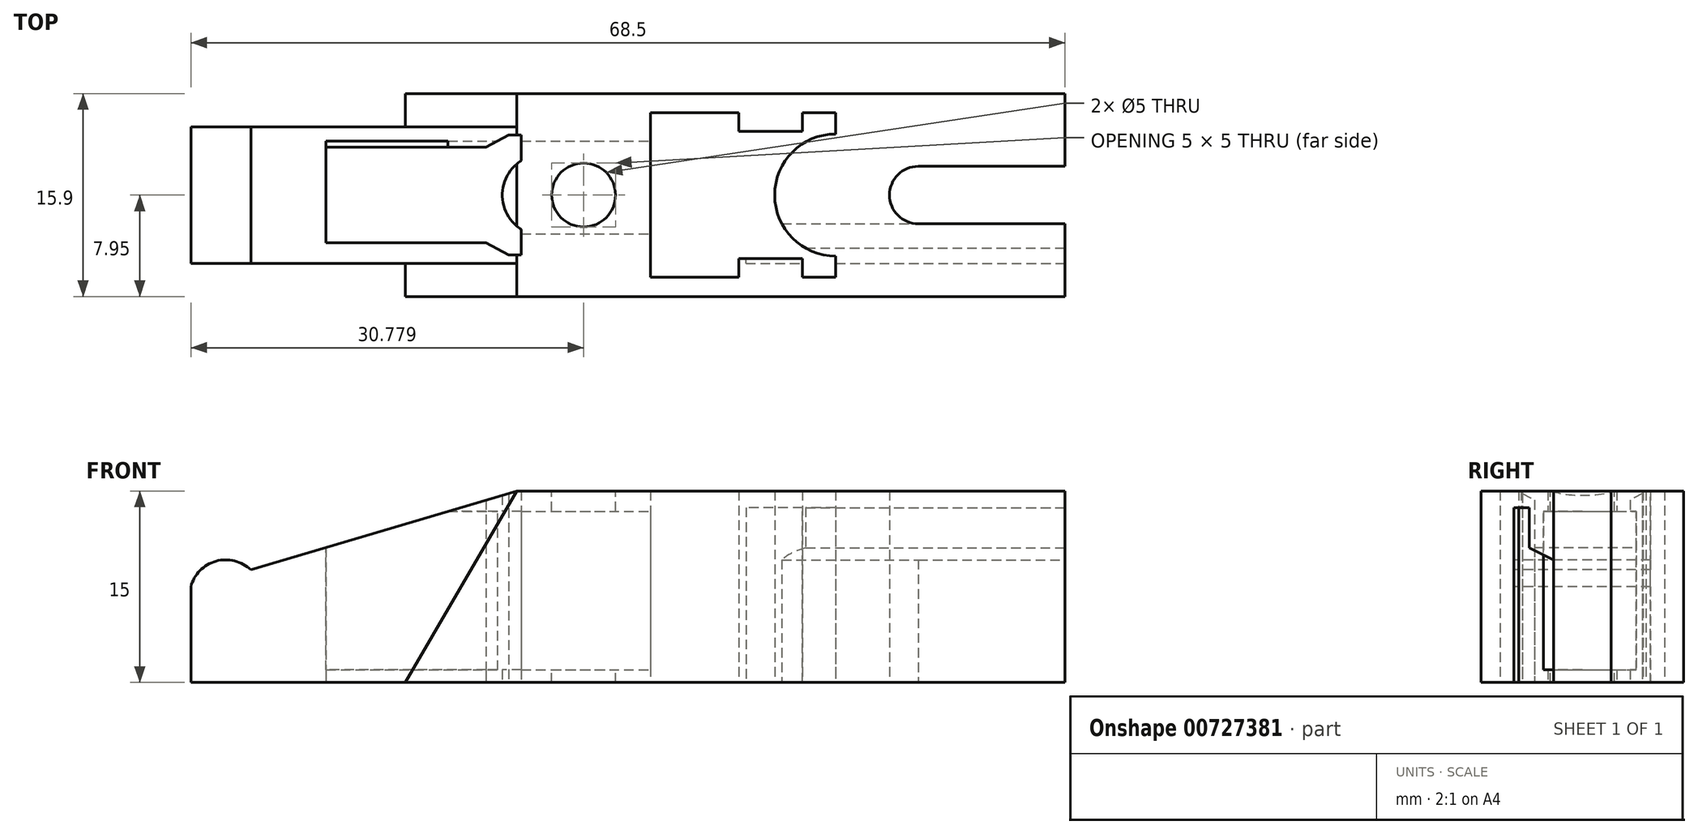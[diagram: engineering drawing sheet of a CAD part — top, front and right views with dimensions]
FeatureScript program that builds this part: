
annotation { "Feature Type Name" : "Feature", "Feature Type Description" : "" }
export const myFeature = defineFeature(function(context is Context, id is Id, definition is map)
    precondition{}
    {
        {
            var Q0;
            Q0=qCreatedBy(makeId("Top.planeOp"),FACE);
            var sketch = newSketch(context, id + "F0", { "sketchPlane" : qUnion([Q0])});
            skLineSegment(sketch, "E0", {"start": v(0, 0) * mm, "end": v(0, 10.7) * mm});
            skLineSegment(sketch, "E1", {"start": v(0, 10.7) * mm, "end": v(16.8, 10.7) * mm});
            skLineSegment(sketch, "E2", {"start": v(68.5, 13.3) * mm, "end": v(68.5, 7.6) * mm});
            skLineSegment(sketch, "E3", {"start": v(68.5, 7.6) * mm, "end": v(57, 7.6) * mm});
            skLineSegment(sketch, "E4", {"start": v(57, 3.1) * mm, "end": v(68.5, 3.1) * mm});
            skLineSegment(sketch, "E5", {"start": v(0, 0) * mm, "end": v(16.8, 0) * mm});
            skLineSegment(sketch, "E6", {"start": v(16.8, 0) * mm, "end": v(16.8, -2.6) * mm});
            skLineSegment(sketch, "E7", {"start": v(16.8, -2.6) * mm, "end": v(68.5, -2.6) * mm});
            skLineSegment(sketch, "E8", {"start": v(68.5, -2.6) * mm, "end": v(68.5, 3.1) * mm});
            skLineSegment(sketch, "E9", {"start": v(50.53, -1.1) * mm, "end": v(50.53, 0.57) * mm});
            skLineSegment(sketch, "E10", {"start": v(25.9, 0.66) * mm, "end": v(25.9, 2.66) * mm});
            skLineSegment(sketch, "E11.MirrorCS", {"start": v(10.6, 9.1) * mm, "end": v(23.13, 9.1) * mm});
            skLineSegment(sketch, "E12.MirrorCS", {"start": v(25.9, 10.04) * mm, "end": v(25.9, 8.04) * mm});
            skArc(sketch, "E13", {"start": v(25.9, 8.04) * mm, "mid": v(24.4, 5.35) * mm, "end": v(25.9, 2.66) * mm});
            skLineSegment(sketch, "E14.MirrorCS", {"start": v(16.8, 10.7) * mm, "end": v(16.8, 13.3) * mm});
            skLineSegment(sketch, "E15.MirrorCS", {"start": v(16.8, 13.3) * mm, "end": v(68.5, 13.3) * mm});
            skLineSegment(sketch, "E16", {"start": v(36.03, -1.1) * mm, "end": v(42.93, -1.1) * mm});
            skLineSegment(sketch, "E17", {"start": v(42.93, -1.1) * mm, "end": v(42.93, 0.37) * mm});
            skLineSegment(sketch, "E18", {"start": v(42.93, 0.37) * mm, "end": v(47.93, 0.37) * mm});
            skLineSegment(sketch, "E19", {"start": v(47.93, 0.37) * mm, "end": v(47.93, -1.1) * mm});
            skLineSegment(sketch, "E20", {"start": v(47.93, -1.1) * mm, "end": v(50.53, -1.1) * mm});
            skLineSegment(sketch, "E21.MirrorCS", {"start": v(23.13, 9.1) * mm, "end": v(24.9, 10.04) * mm});
            skLineSegment(sketch, "E22.MirrorCS", {"start": v(24.9, 10.04) * mm, "end": v(25.9, 10.04) * mm});
            skPoint(sketch, "E23", {"position": v(24.4, 5.35) * mm});
            skLineSegment(sketch, "E24", {"start": v(57, 7.6) * mm, "end": v(57, 3.1) * mm, "construction": true});
            skArc(sketch, "E25", {"start": v(57, 7.6) * mm, "mid": v(54.75, 5.35) * mm, "end": v(57, 3.1) * mm});
            skLineSegment(sketch, "E26", {"start": v(0, 5.35) * mm, "end": v(68.5, 5.35) * mm, "construction": true});
            skLineSegment(sketch, "E27.MirrorCS", {"start": v(10.6, 1.6) * mm, "end": v(23.13, 1.6) * mm});
            skLineSegment(sketch, "E28.MirrorCS", {"start": v(23.13, 1.6) * mm, "end": v(24.9, 0.66) * mm});
            skLineSegment(sketch, "E29.MirrorCS", {"start": v(24.9, 0.66) * mm, "end": v(25.9, 0.66) * mm});
            skLineSegment(sketch, "E30", {"start": v(10.6, 9.1) * mm, "end": v(10.6, 1.6) * mm});
            skLineSegment(sketch, "E31", {"start": v(36.03, 11.8) * mm, "end": v(36.03, -1.1) * mm});
            skLineSegment(sketch, "E32.MirrorCS", {"start": v(36.03, 11.8) * mm, "end": v(42.93, 11.8) * mm});
            skLineSegment(sketch, "E33.MirrorCS", {"start": v(42.93, 11.8) * mm, "end": v(42.93, 10.33) * mm});
            skLineSegment(sketch, "E34.MirrorCS", {"start": v(42.93, 10.33) * mm, "end": v(47.93, 10.33) * mm});
            skLineSegment(sketch, "E35.MirrorCS", {"start": v(47.93, 10.33) * mm, "end": v(47.93, 11.8) * mm});
            skLineSegment(sketch, "E36.MirrorCS", {"start": v(47.93, 11.8) * mm, "end": v(50.53, 11.8) * mm});
            skLineSegment(sketch, "E37.MirrorCS", {"start": v(50.53, 11.8) * mm, "end": v(50.53, 10.13) * mm});
            skLineSegment(sketch, "E38", {"start": v(50.53, 10.13) * mm, "end": v(50.53, 0.57) * mm, "construction": true});
            skArc(sketch, "E39", {"start": v(50.53, 10.13) * mm, "mid": v(45.75, 5.35) * mm, "end": v(50.53, 0.57) * mm});
            skPoint(sketch, "E40", {"position": v(45.75, 5.35) * mm});
            skSolve(sketch);
        }
        {
            var Q0;
            Q0=qSketchRegion(id+"F0",true);
            var Q1;
            Q1=makeQuery(id+"F0.imprint","IMPRINT",FACE,{"disambiguationData":[TD([[makeQuery(id+"F0.imprint","IMPRINT",EDGE,{"derivedFrom":sQuery(id+"F0.wireOp",EDGE,"E0")}),-1.0]])]});
            extrude(context, id + "F1", {"entities" : qUnion([Q0, Q1]), "depth" : 15 * mm, "offsetDistance" : 25 * mm});
        }
        {
            var Q0;
            Q0=makeQuery(id+"F1.opExtrude","SWEPT_FACE",FACE,{"disambiguationData":[OSD([sQuery(id+"F0.wireOp",EDGE,"E7")])]});
            var sketch = newSketch(context, id + "F2", { "sketchPlane" : qUnion([Q0])});
            skLineSegment(sketch, "E41", {"start": v(16.8, 0) * mm, "end": v(25.53, 15) * mm});
            skLineSegment(sketch, "E42", {"start": v(25.53, 15) * mm, "end": v(16.8, 15) * mm});
            skLineSegment(sketch, "E43", {"start": v(16.8, 15) * mm, "end": v(16.8, 0) * mm});
            skSolve(sketch);
        }
        {
            var Q0;
            Q0=qSketchRegion(id+"F2",true);
            var Q1;
            Q1=makeQuery(id+"F1.opExtrude","SWEPT_FACE",FACE,{"disambiguationData":[OSD([sQuery(id+"F0.wireOp",EDGE,"E5")])]});
            extrude(context, id + "F3", {"entities" : qUnion([Q0]), "operationType" : NewBodyOperationType.REMOVE, "endBound" : BoundingType.UP_TO_SURFACE, "oppositeDirection" : true, "depth" : 25 * mm, "endBoundEntityFace" : qUnion([Q1]), "offsetDistance" : 25 * mm});
        }
        {
            var Q0;
            Q0=makeQuery(id+"F1.opExtrude","SWEPT_FACE",FACE,{"disambiguationData":[OSD([sQuery(id+"F0.wireOp",EDGE,"E15.MirrorCS")])]});
            var sketch = newSketch(context, id + "F4", { "sketchPlane" : qUnion([Q0])});
            skLineSegment(sketch, "E44", {"start": v(-16.8, 0) * mm, "end": v(-16.8, 15) * mm});
            skLineSegment(sketch, "E45", {"start": v(-16.8, 15) * mm, "end": v(-25.53, 15) * mm});
            skLineSegment(sketch, "E46", {"start": v(-25.53, 15) * mm, "end": v(-16.8, 0) * mm});
            skSolve(sketch);
        }
        {
            var Q0;
            Q0=qSketchRegion(id+"F4",true);
            var Q1;
            Q1=makeQuery(id+"F1.opExtrude","SWEPT_FACE",FACE,{"disambiguationData":[OSD([sQuery(id+"F0.wireOp",EDGE,"E1")])]});
            extrude(context, id + "F5", {"entities" : qUnion([Q0]), "operationType" : NewBodyOperationType.REMOVE, "endBound" : BoundingType.UP_TO_SURFACE, "oppositeDirection" : true, "depth" : 25 * mm, "endBoundEntityFace" : qUnion([Q1]), "offsetDistance" : 25 * mm});
        }
        {
            var Q0;
            Q0=makeQuery(id+"F1.opExtrude","CAP_FACE",FACE,{"disambiguationData":[OSD([sQuery(id+"F0.wireOp",EDGE,"E0"),sQuery(id+"F0.wireOp",EDGE,"E1"),sQuery(id+"F0.wireOp",EDGE,"E2"),sQuery(id+"F0.wireOp",EDGE,"E3"),sQuery(id+"F0.wireOp",EDGE,"E4"),sQuery(id+"F0.wireOp",EDGE,"E5"),sQuery(id+"F0.wireOp",EDGE,"E6"),sQuery(id+"F0.wireOp",EDGE,"E7"),sQuery(id+"F0.wireOp",EDGE,"E8"),sQuery(id+"F0.wireOp",EDGE,"E9"),sQuery(id+"F0.wireOp",EDGE,"E10"),sQuery(id+"F0.wireOp",EDGE,"E11.MirrorCS"),sQuery(id+"F0.wireOp",EDGE,"E12.MirrorCS"),sQuery(id+"F0.wireOp",EDGE,"E13"),sQuery(id+"F0.wireOp",EDGE,"E14.MirrorCS"),sQuery(id+"F0.wireOp",EDGE,"E15.MirrorCS"),sQuery(id+"F0.wireOp",EDGE,"E16"),sQuery(id+"F0.wireOp",EDGE,"E17"),sQuery(id+"F0.wireOp",EDGE,"E18"),sQuery(id+"F0.wireOp",EDGE,"E19"),sQuery(id+"F0.wireOp",EDGE,"E20"),sQuery(id+"F0.wireOp",EDGE,"E21.MirrorCS"),sQuery(id+"F0.wireOp",EDGE,"E22.MirrorCS"),sQuery(id+"F0.wireOp",EDGE,"E25"),sQuery(id+"F0.wireOp",EDGE,"E27.MirrorCS"),sQuery(id+"F0.wireOp",EDGE,"E28.MirrorCS"),sQuery(id+"F0.wireOp",EDGE,"E29.MirrorCS"),sQuery(id+"F0.wireOp",EDGE,"E30"),sQuery(id+"F0.wireOp",EDGE,"E31"),sQuery(id+"F0.wireOp",EDGE,"E32.MirrorCS"),sQuery(id+"F0.wireOp",EDGE,"E33.MirrorCS"),sQuery(id+"F0.wireOp",EDGE,"E34.MirrorCS"),sQuery(id+"F0.wireOp",EDGE,"E35.MirrorCS"),sQuery(id+"F0.wireOp",EDGE,"E36.MirrorCS"),sQuery(id+"F0.wireOp",EDGE,"E37.MirrorCS"),sQuery(id+"F0.wireOp",EDGE,"E39")])],"isStart":false});
            var sketch = newSketch(context, id + "F6", { "sketchPlane" : qUnion([Q0])});
            skCircle(sketch, "E47", {"center": v(30.78, 5.35) * mm, "radius": 2.5 * mm});
            skPoint(sketch, "E47.centerSnap0", {"position": v(36.03, 5.35) * mm});
            skSolve(sketch);
        }
        {
            var Q0;
            Q0=qSketchRegion(id+"F6",true);
            extrude(context, id + "F7", {"entities" : qUnion([Q0]), "operationType" : NewBodyOperationType.REMOVE, "endBound" : BoundingType.THROUGH_ALL, "oppositeDirection" : true, "depth" : 25 * mm, "offsetDistance" : 25 * mm});
        }
        {
            var Q0;
            Q0=makeQuery(id+"F1.opExtrude","SWEPT_FACE",FACE,{"disambiguationData":[OSD([sQuery(id+"F0.wireOp",EDGE,"E8")])]});
            var sketch = newSketch(context, id + "F8", { "sketchPlane" : qUnion([Q0])});
            skLineSegment(sketch, "E48", {"start": v(0, 0) * mm, "end": v(0, 13.7) * mm});
            skLineSegment(sketch, "E49", {"start": v(0, 13.7) * mm, "end": v(1.18, 13.7) * mm});
            skLineSegment(sketch, "E50", {"start": v(1.18, 13.7) * mm, "end": v(1.18, 10.55) * mm});
            skLineSegment(sketch, "E51", {"start": v(1.18, 10.55) * mm, "end": v(3.1, 9.61) * mm});
            skLineSegment(sketch, "E52", {"start": v(3.1, 9.61) * mm, "end": v(3.1, 11.46) * mm});
            skLineSegment(sketch, "E53", {"start": v(3.1, 11.46) * mm, "end": v(2.48, 11.7) * mm});
            skLineSegment(sketch, "E54", {"start": v(2.48, 11.7) * mm, "end": v(2.48, 15) * mm});
            skLineSegment(sketch, "E55", {"start": v(2.48, 15) * mm, "end": v(-2.6, 15) * mm});
            skLineSegment(sketch, "E56", {"start": v(-2.6, 15) * mm, "end": v(-2.6, 0) * mm});
            skLineSegment(sketch, "E57", {"start": v(5.37, 15.07) * mm, "end": v(5.37, -0.31) * mm, "construction": true});
            skLineSegment(sketch, "E58.MirrorCS", {"start": v(8.27, 11.7) * mm, "end": v(8.27, 15) * mm});
            skLineSegment(sketch, "E59.MirrorCS", {"start": v(7.65, 11.46) * mm, "end": v(8.27, 11.7) * mm});
            skLineSegment(sketch, "E60.MirrorCS", {"start": v(9.57, 10.55) * mm, "end": v(7.65, 9.61) * mm});
            skLineSegment(sketch, "E61.MirrorCS", {"start": v(9.57, 13.7) * mm, "end": v(9.57, 10.55) * mm});
            skLineSegment(sketch, "E62.MirrorCS", {"start": v(10.75, 13.7) * mm, "end": v(9.57, 13.7) * mm});
            skLineSegment(sketch, "E63.MirrorCS", {"start": v(10.75, 0) * mm, "end": v(10.75, 13.7) * mm});
            skLineSegment(sketch, "E64.MirrorCS", {"start": v(13.35, 15) * mm, "end": v(13.35, 0) * mm});
            skLineSegment(sketch, "E65.MirrorCS", {"start": v(8.27, 15) * mm, "end": v(13.35, 15) * mm});
            skLineSegment(sketch, "E66", {"start": v(-2.6, 0) * mm, "end": v(0, 0) * mm});
            skSolve(sketch);
        }
        {
            var Q0;
            {var subQ5=sQuery(id+"F8.wireOp",EDGE,"E48");Q0=makeQuery(id+"F8.imprint","IMPRINT",FACE,{"disambiguationData":[TD([[makeQuery(id+"F8.imprint","IMPRINT",EDGE,{"derivedFrom":subQ5}),-1.0]])]});}
            extrude(context, id + "F9", {"entities" : qUnion([Q0]), "operationType" : NewBodyOperationType.REMOVE, "oppositeDirection" : true, "depth" : 25 * mm, "offsetDistance" : 25 * mm});
        }
        {
            var Q0;
            Q0=makeQuery(id+"F1.opExtrude","SWEPT_FACE",FACE,{"disambiguationData":[OSD([sQuery(id+"F0.wireOp",EDGE,"E31")])]});
            var sketch = newSketch(context, id + "F10", { "sketchPlane" : qUnion([Q0])});
            skLineSegment(sketch, "E67.bottom", {"start": v(2.32, 13.4) * mm, "end": v(9.58, 13.4) * mm});
            skLineSegment(sketch, "E67.top", {"start": v(2.32, 0.98) * mm, "end": v(9.58, 0.98) * mm});
            skLineSegment(sketch, "E67.left", {"start": v(2.32, 13.4) * mm, "end": v(2.32, 0.98) * mm});
            skLineSegment(sketch, "E67.right", {"start": v(9.58, 13.4) * mm, "end": v(9.58, 0.98) * mm});
            skSolve(sketch);
        }
        {
            var Q0;
            Q0=qSketchRegion(id+"F10",true);
            var Q1;
            Q1=makeQuery(id+"F1.opExtrude","SWEPT_FACE",FACE,{"disambiguationData":[OSD([sQuery(id+"F0.wireOp",EDGE,"E30")])]});
            extrude(context, id + "F11", {"entities" : qUnion([Q0]), "operationType" : NewBodyOperationType.REMOVE, "endBound" : BoundingType.UP_TO_SURFACE, "oppositeDirection" : true, "depth" : 25 * mm, "endBoundEntityFace" : qUnion([Q1]), "offsetDistance" : 25 * mm});
        }
        {
            var Q0;
            {var subQ0=sQuery(id+"F0.wireOp",EDGE,"E5");Q0=makeQuery(id+"F3.boolean.opBoolean","MERGE",FACE,{"derivedFrom":[makeQuery(id+"F1.opExtrude","SWEPT_FACE",FACE,{"disambiguationData":[OSD([subQ0])]}),makeQuery(id+"F3.opExtrude","CAP_FACE",FACE,{"disambiguationData":[OSD([subQ0])],"isStart":false})]});}
            var sketch = newSketch(context, id + "F12", { "sketchPlane" : qUnion([Q0])});
            skArc(sketch, "E68", {"start": v(4.7, 8.82) * mm, "mid": v(1.97, 9.5) * mm, "end": v(0, 7.5) * mm});
            skLineSegment(sketch, "E69", {"start": v(4.7, 8.82) * mm, "end": v(25.53, 15) * mm});
            skLineSegment(sketch, "E70", {"start": v(25.53, 15) * mm, "end": v(16.8, 0) * mm});
            skLineSegment(sketch, "E71", {"start": v(16.8, 0) * mm, "end": v(0, 0) * mm});
            skLineSegment(sketch, "E72", {"start": v(0, 0) * mm, "end": v(0, 7.5) * mm});
            skSolve(sketch);
        }
        {
            var Q0;
            {var subQ0=sQuery(id+"F12.wireOp",EDGE,"E68");Q0=makeQuery(id+"F12.imprint","IMPRINT",FACE,{"disambiguationData":[TD([[makeQuery(id+"F12.imprint","IMPRINT",EDGE,{"derivedFrom":subQ0}),-1.0]])]});}
            extrude(context, id + "F13", {"entities" : qUnion([Q0]), "operationType" : NewBodyOperationType.REMOVE, "endBound" : BoundingType.THROUGH_ALL, "oppositeDirection" : true, "depth" : 25 * mm, "offsetDistance" : 25 * mm});
        }
    });
